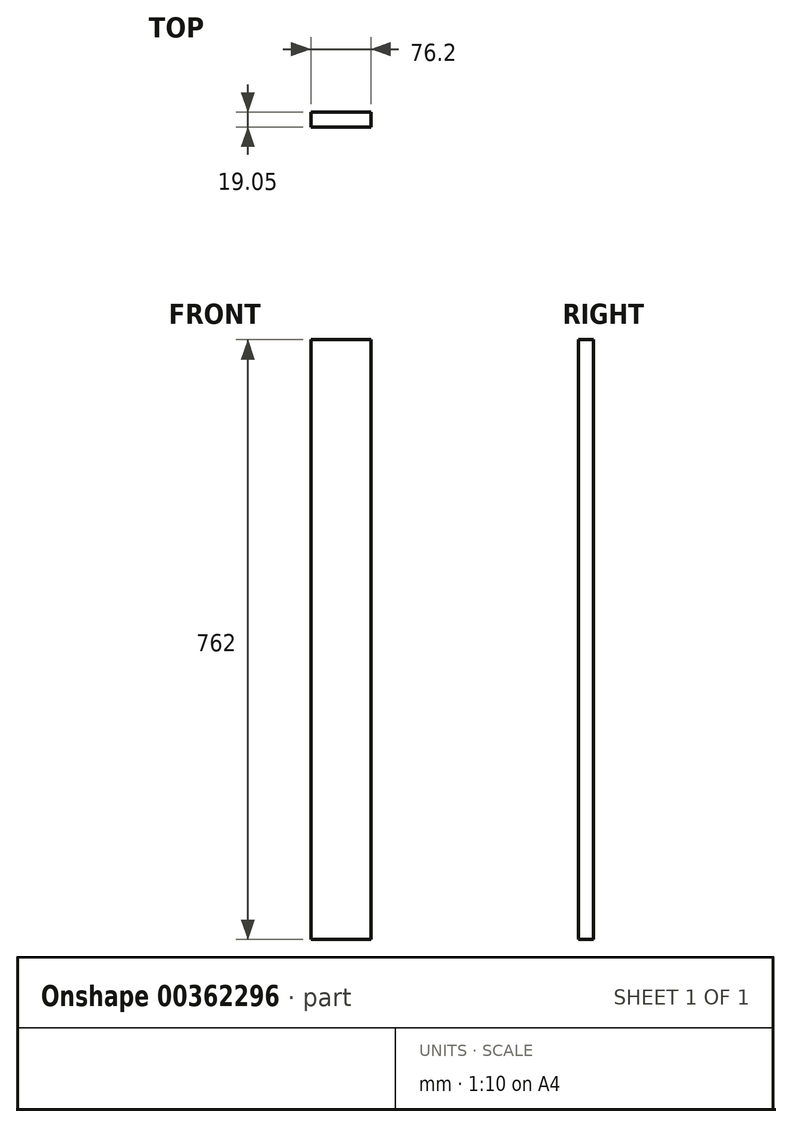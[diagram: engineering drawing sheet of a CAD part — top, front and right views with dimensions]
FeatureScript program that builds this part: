
annotation { "Feature Type Name" : "Feature", "Feature Type Description" : "" }
export const myFeature = defineFeature(function(context is Context, id is Id, definition is map)
    precondition{}
    {
        {
            var Q0;
            Q0=qCreatedBy(makeId("Front.planeOp"),FACE);
            var sketch = newSketch(context, id + "F0", { "sketchPlane" : qUnion([Q0])});
            skLineSegment(sketch, "E0.bottom", {"start": v(-66.05, 241.43) * mm, "end": v(10.15, 241.43) * mm});
            skLineSegment(sketch, "E0.top", {"start": v(-66.05, -520.57) * mm, "end": v(10.15, -520.57) * mm});
            skLineSegment(sketch, "E0.left", {"start": v(-66.05, 241.43) * mm, "end": v(-66.05, -520.57) * mm});
            skLineSegment(sketch, "E0.right", {"start": v(10.15, 241.43) * mm, "end": v(10.15, -520.57) * mm});
            skSolve(sketch);
        }
        {
            var Q0;
            Q0=makeQuery(id+"F0.imprint","IMPRINT",FACE,{"disambiguationData":[TD([[makeQuery(id+"F0.imprint","IMPRINT",EDGE,{"derivedFrom":sQuery(id+"F0.wireOp",EDGE,"E0.bottom")}),-1.0]])]});
            extrude(context, id + "F1", {"entities" : qUnion([Q0]), "depth" : 19.05 * mm});
        }
    });
